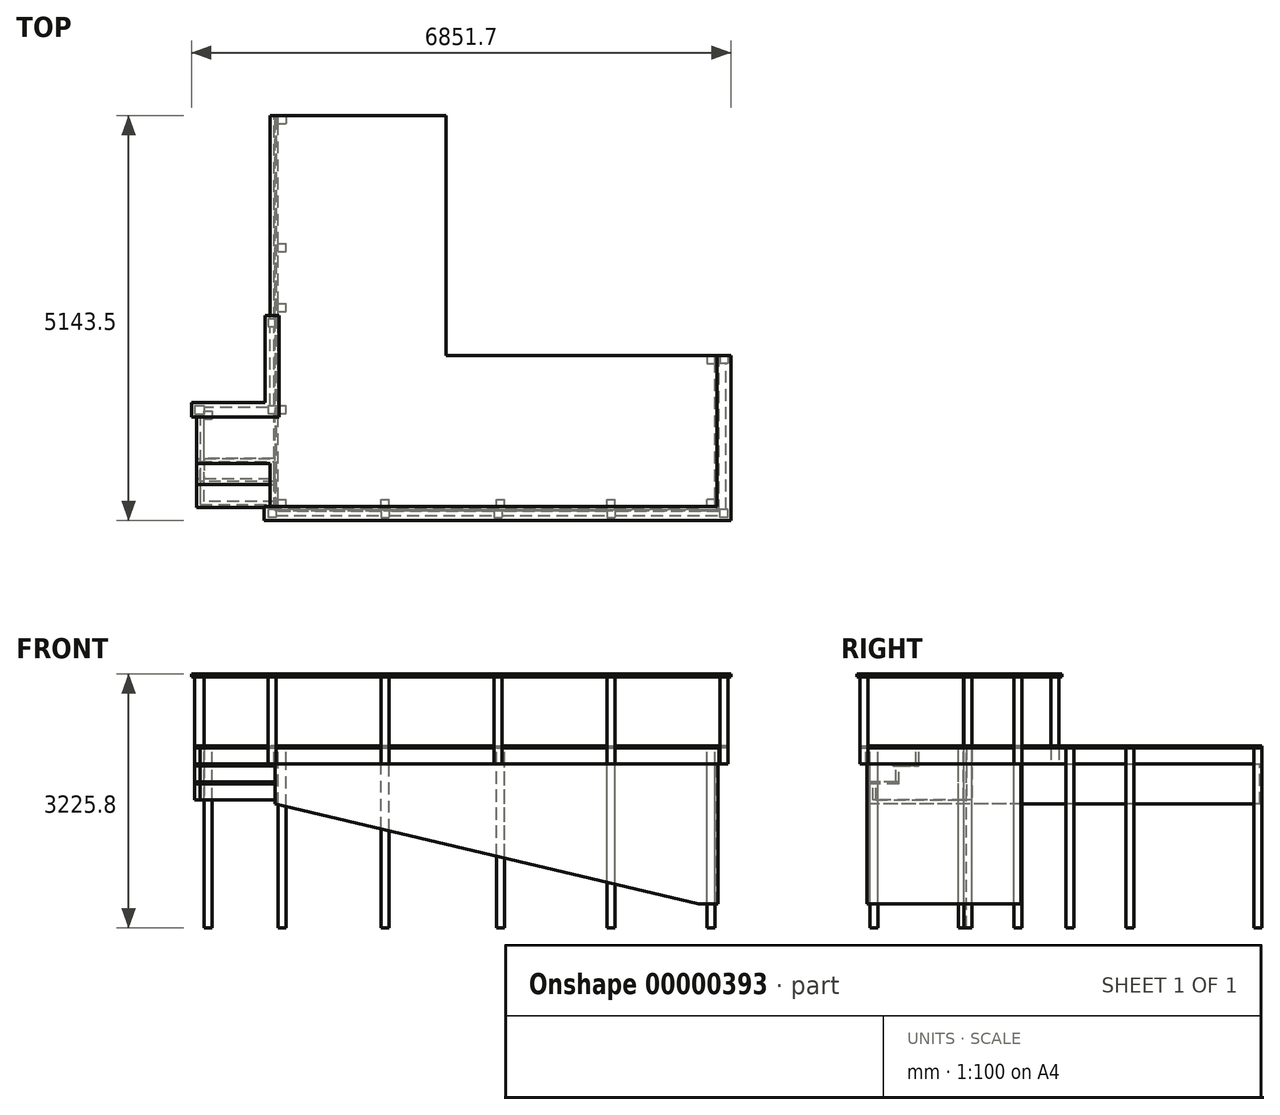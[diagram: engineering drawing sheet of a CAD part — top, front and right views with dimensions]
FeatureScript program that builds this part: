
annotation { "Feature Type Name" : "Feature", "Feature Type Description" : "" }
export const myFeature = defineFeature(function(context is Context, id is Id, definition is map)
    precondition{}
    {
        {
            var Q0;
            Q0=qCreatedBy(makeId("Top.planeOp"),FACE);
            var sketch = newSketch(context, id + "F0", { "sketchPlane" : qUnion([Q0])});
            skLineSegment(sketch, "E0.bottom", {"start": v(0, 0) * mm, "end": v(5791.2, 0) * mm});
            skLineSegment(sketch, "E0.top", {"start": v(2235.2, 2032) * mm, "end": v(5791.2, 2032) * mm});
            skLineSegment(sketch, "E0.right", {"start": v(5791.2, 0) * mm, "end": v(5791.2, 2032) * mm});
            skLineSegment(sketch, "E1.top", {"start": v(2235.2, 5080) * mm, "end": v(0, 5080) * mm});
            skLineSegment(sketch, "E1.left", {"start": v(2235.2, 2032) * mm, "end": v(2235.2, 5080) * mm});
            skLineSegment(sketch, "E2", {"start": v(0, 0) * mm, "end": v(0, 5080) * mm});
            skSolve(sketch);
        }
        {
            var Q0;
            Q0=makeQuery(id+"F0.imprint","IMPRINT",FACE,{"disambiguationData":[TD([[makeQuery(id+"F0.imprint","IMPRINT",EDGE,{"derivedFrom":sQuery(id+"F0.wireOp",EDGE,"E0.bottom")}),1.0]])]});
            extrude(context, id + "F1", {"entities" : qUnion([Q0]), "depth" : 25.4 * mm});
        }
        {
            var Q0;
            Q0=makeQuery(id+"F1.opExtrude","CAP_FACE",FACE,{"disambiguationData":[OSD([sQuery(id+"F0.wireOp",EDGE,"E0.bottom"),sQuery(id+"F0.wireOp",EDGE,"E0.top"),sQuery(id+"F0.wireOp",EDGE,"E0.right"),sQuery(id+"F0.wireOp",EDGE,"E1.top"),sQuery(id+"F0.wireOp",EDGE,"E1.left"),sQuery(id+"F0.wireOp",EDGE,"E2")])],"isStart":true});
            var sketch = newSketch(context, id + "F2", { "sketchPlane" : qUnion([Q0])});
            skLineSegment(sketch, "E3.bottom", {"start": v(5701.33, -50.8) * mm, "end": v(50.8, -50.8) * mm});
            skLineSegment(sketch, "E3.top", {"start": v(5650.53, -101.6) * mm, "end": v(101.6, -101.6) * mm});
            skLineSegment(sketch, "E3.left", {"start": v(5701.33, -50.8) * mm, "end": v(5701.33, -101.6) * mm});
            skLineSegment(sketch, "E3.right", {"start": v(50.8, -50.8) * mm, "end": v(50.8, -101.6) * mm});
            skLineSegment(sketch, "E4.top", {"start": v(50.8, -5080) * mm, "end": v(101.6, -5080) * mm});
            skLineSegment(sketch, "E4.left", {"start": v(50.8, -101.6) * mm, "end": v(50.8, -5080) * mm});
            skLineSegment(sketch, "E4.right", {"start": v(101.6, -101.6) * mm, "end": v(101.6, -5080) * mm});
            skLineSegment(sketch, "E5.top", {"start": v(5701.33, -2032) * mm, "end": v(5650.53, -2032) * mm});
            skLineSegment(sketch, "E5.left", {"start": v(5701.33, -101.6) * mm, "end": v(5701.33, -2032) * mm});
            skLineSegment(sketch, "E5.right", {"start": v(5650.53, -101.6) * mm, "end": v(5650.53, -2032) * mm});
            skSolve(sketch);
        }
        {
            var Q0;
            Q0=makeQuery(id+"F2.imprint","IMPRINT",FACE,{"disambiguationData":[TD([[makeQuery(id+"F2.imprint","IMPRINT",EDGE,{"derivedFrom":sQuery(id+"F2.wireOp",EDGE,"E3.bottom")}),1.0]])]});
            extrude(context, id + "F3", {"entities" : qUnion([Q0]), "operationType" : NewBodyOperationType.ADD, "depth" : 203.2 * mm});
        }
        {
            var Q0;
            Q0=makeQuery(id+"F1.opExtrude","CAP_FACE",FACE,{"disambiguationData":[OSD([sQuery(id+"F0.wireOp",EDGE,"E0.bottom"),sQuery(id+"F0.wireOp",EDGE,"E0.top"),sQuery(id+"F0.wireOp",EDGE,"E0.right"),sQuery(id+"F0.wireOp",EDGE,"E1.top"),sQuery(id+"F0.wireOp",EDGE,"E1.left"),sQuery(id+"F0.wireOp",EDGE,"E2")])],"isStart":false});
            var sketch = newSketch(context, id + "F4", { "sketchPlane" : qUnion([Q0])});
            skLineSegment(sketch, "E6.bottom", {"start": v(5816.6, -25.4) * mm, "end": v(5715, -25.4) * mm});
            skLineSegment(sketch, "E6.top", {"start": v(5816.6, 76.2) * mm, "end": v(5715, 76.2) * mm});
            skLineSegment(sketch, "E6.left", {"start": v(5816.6, -25.4) * mm, "end": v(5816.6, 76.2) * mm});
            skLineSegment(sketch, "E6.right", {"start": v(5715, -25.4) * mm, "end": v(5715, 76.2) * mm});
            skLineSegment(sketch, "E7.bottom", {"start": v(5816.6, 2032) * mm, "end": v(5715, 2032) * mm});
            skLineSegment(sketch, "E7.top", {"start": v(5816.6, 1930.4) * mm, "end": v(5715, 1930.4) * mm});
            skLineSegment(sketch, "E7.left", {"start": v(5816.6, 2032) * mm, "end": v(5816.6, 1930.4) * mm});
            skLineSegment(sketch, "E7.right", {"start": v(5715, 2032) * mm, "end": v(5715, 1930.4) * mm});
            skLineSegment(sketch, "E8.bottom", {"start": v(4279.9, 76.2) * mm, "end": v(4381.5, 76.2) * mm});
            skLineSegment(sketch, "E8.top", {"start": v(4279.9, -25.4) * mm, "end": v(4381.5, -25.4) * mm});
            skLineSegment(sketch, "E8.left", {"start": v(4279.9, 76.2) * mm, "end": v(4279.9, -25.4) * mm});
            skLineSegment(sketch, "E8.right", {"start": v(4381.5, 76.2) * mm, "end": v(4381.5, -25.4) * mm});
            skLineSegment(sketch, "E9.bottom", {"start": v(2844.8, 76.2) * mm, "end": v(2946.4, 76.2) * mm});
            skLineSegment(sketch, "E9.top", {"start": v(2844.8, -25.4) * mm, "end": v(2946.4, -25.4) * mm});
            skLineSegment(sketch, "E9.left", {"start": v(2844.8, 76.2) * mm, "end": v(2844.8, -25.4) * mm});
            skLineSegment(sketch, "E9.right", {"start": v(2946.4, 76.2) * mm, "end": v(2946.4, -25.4) * mm});
            skLineSegment(sketch, "E10.bottom", {"start": v(1409.7, 76.2) * mm, "end": v(1511.3, 76.2) * mm});
            skLineSegment(sketch, "E10.top", {"start": v(1409.7, -25.4) * mm, "end": v(1511.3, -25.4) * mm});
            skLineSegment(sketch, "E10.left", {"start": v(1409.7, 76.2) * mm, "end": v(1409.7, -25.4) * mm});
            skLineSegment(sketch, "E10.right", {"start": v(1511.3, 76.2) * mm, "end": v(1511.3, -25.4) * mm});
            skLineSegment(sketch, "E11.bottom", {"start": v(76.2, 76.2) * mm, "end": v(-25.4, 76.2) * mm});
            skLineSegment(sketch, "E11.top", {"start": v(76.2, -25.4) * mm, "end": v(-25.4, -25.4) * mm});
            skLineSegment(sketch, "E11.left", {"start": v(76.2, 76.2) * mm, "end": v(76.2, -25.4) * mm});
            skLineSegment(sketch, "E11.right", {"start": v(-25.4, 76.2) * mm, "end": v(-25.4, -25.4) * mm});
            skLineSegment(sketch, "E12.bottom", {"start": v(-25.4, 1397) * mm, "end": v(76.2, 1397) * mm});
            skLineSegment(sketch, "E12.top", {"start": v(-25.4, 1295.4) * mm, "end": v(76.2, 1295.4) * mm});
            skLineSegment(sketch, "E12.left", {"start": v(-25.4, 1397) * mm, "end": v(-25.4, 1295.4) * mm});
            skLineSegment(sketch, "E12.right", {"start": v(76.2, 1397) * mm, "end": v(76.2, 1295.4) * mm});
            skLineSegment(sketch, "E13.bottom", {"start": v(-25.4, 2500.64) * mm, "end": v(76.2, 2500.64) * mm});
            skLineSegment(sketch, "E13.top", {"start": v(-25.4, 2399.04) * mm, "end": v(76.2, 2399.04) * mm});
            skLineSegment(sketch, "E13.left", {"start": v(-25.4, 2500.64) * mm, "end": v(-25.4, 2399.04) * mm});
            skLineSegment(sketch, "E13.right", {"start": v(76.2, 2500.64) * mm, "end": v(76.2, 2399.04) * mm});
            skLineSegment(sketch, "E14.bottom", {"start": v(-958.9, 1397) * mm, "end": v(-838.2, 1397) * mm});
            skLineSegment(sketch, "E14.top", {"start": v(-958.9, 1290.4) * mm, "end": v(-838.2, 1290.4) * mm});
            skLineSegment(sketch, "E14.left", {"start": v(-958.9, 1397) * mm, "end": v(-958.9, 1290.4) * mm});
            skLineSegment(sketch, "E14.right", {"start": v(-838.2, 1397) * mm, "end": v(-838.2, 1290.4) * mm});
            skLineSegment(sketch, "E15", {"start": v(76.2, 76.2) * mm, "end": v(1409.7, 76.2) * mm, "construction": true});
            skLineSegment(sketch, "E16", {"start": v(2844.8, 76.2) * mm, "end": v(1511.3, 76.2) * mm, "construction": true});
            skLineSegment(sketch, "E17", {"start": v(4279.9, 76.2) * mm, "end": v(2946.4, 76.2) * mm, "construction": true});
            skLineSegment(sketch, "E18", {"start": v(5715, 76.2) * mm, "end": v(4381.5, 76.2) * mm, "construction": true});
            skSolve(sketch);
        }
        {
            var Q0;
            {var subQ6=sQuery(id+"F4.wireOp",EDGE,"E7.left");var subQ13=sQuery(id+"F4.wireOp",EDGE,"E8.top");var subQ19=sQuery(id+"F4.wireOp",EDGE,"E9.top");var subQ22=sQuery(id+"F4.wireOp",EDGE,"E10.top");var subQ32=sQuery(id+"F4.wireOp",EDGE,"E12.left");var subQ38=sQuery(id+"F4.wireOp",EDGE,"E13.left");var subQ39=sQuery(id+"F4.wireOp",EDGE,"E7.right");var subQ40=sQuery(id+"F4.wireOp",EDGE,"E8.bottom");var subQ41=sQuery(id+"F4.wireOp",EDGE,"E9.bottom");var subQ42=sQuery(id+"F4.wireOp",EDGE,"E10.bottom");var subQ43=sQuery(id+"F4.wireOp",EDGE,"E12.right");var subQ44=sQuery(id+"F4.wireOp",EDGE,"E13.right");var subQ45=sQuery(id+"F4.wireOp",EDGE,"E6.right");var subQ49=sQuery(id+"F4.wireOp",EDGE,"E6.bottom");var subQ50=sQuery(id+"F4.wireOp",EDGE,"E6.top");var subQ54=sQuery(id+"F4.wireOp",EDGE,"E11.bottom");var subQ58=sQuery(id+"F4.wireOp",EDGE,"E11.left");var subQ62=sQuery(id+"F4.wireOp",EDGE,"E11.top");var subQ63=makeQuery(id+"F4.imprint","INTERSECT",VERTEX,{"derivedFrom":[subQ50,subQ45]});var subQ64=makeQuery(id+"F4.imprint","INTERSECT",VERTEX,{"derivedFrom":[subQ54,subQ58]});Q0=qUnion([makeQuery(id+"F4.imprint","IMPRINT",FACE,{"disambiguationData":[TD([[makeQuery(id+"F4.imprint","IMPRINT",EDGE,{"derivedFrom":sQuery(id+"F4.wireOp",EDGE,"E14.bottom")}),-1.0]])]}),makeQuery(id+"F4.imprint","IMPRINT",FACE,{"disambiguationData":[TD([[makeQuery(id+"F4.imprint","IMPRINT",EDGE,{"derivedFrom":subQ6}),-1.0]])]}),makeQuery(id+"F4.imprint","IMPRINT",FACE,{"disambiguationData":[TD([[makeQuery(id+"F4.imprint","IMPRINT",EDGE,{"derivedFrom":subQ13}),1.0]])]}),makeQuery(id+"F4.imprint","IMPRINT",FACE,{"disambiguationData":[TD([[makeQuery(id+"F4.imprint","IMPRINT",EDGE,{"derivedFrom":subQ19}),1.0]])]}),makeQuery(id+"F4.imprint","IMPRINT",FACE,{"disambiguationData":[TD([[makeQuery(id+"F4.imprint","IMPRINT",EDGE,{"derivedFrom":subQ22}),1.0]])]}),makeQuery(id+"F4.imprint","IMPRINT",FACE,{"disambiguationData":[TD([[makeQuery(id+"F4.imprint","IMPRINT",EDGE,{"derivedFrom":subQ32}),1.0]])]}),makeQuery(id+"F4.imprint","IMPRINT",FACE,{"disambiguationData":[TD([[makeQuery(id+"F4.imprint","IMPRINT",EDGE,{"derivedFrom":subQ38}),1.0]])]}),makeQuery(id+"F4.imprint","IMPRINT",FACE,{"disambiguationData":[TD([[makeQuery(id+"F4.imprint","IMPRINT",EDGE,{"derivedFrom":subQ39}),1.0]])]}),makeQuery(id+"F4.imprint","IMPRINT",FACE,{"disambiguationData":[TD([[makeQuery(id+"F4.imprint","IMPRINT",EDGE,{"derivedFrom":subQ40}),-1.0]])]}),makeQuery(id+"F4.imprint","IMPRINT",FACE,{"disambiguationData":[TD([[makeQuery(id+"F4.imprint","IMPRINT",EDGE,{"derivedFrom":subQ41}),-1.0]])]}),makeQuery(id+"F4.imprint","IMPRINT",FACE,{"disambiguationData":[TD([[makeQuery(id+"F4.imprint","IMPRINT",EDGE,{"derivedFrom":subQ42}),-1.0]])]}),makeQuery(id+"F4.imprint","IMPRINT",FACE,{"disambiguationData":[TD([[makeQuery(id+"F4.imprint","IMPRINT",EDGE,{"derivedFrom":subQ43}),-1.0]])]}),makeQuery(id+"F4.imprint","IMPRINT",FACE,{"disambiguationData":[TD([[makeQuery(id+"F4.imprint","IMPRINT",EDGE,{"derivedFrom":subQ44}),-1.0]])]}),makeQuery(id+"F4.imprint","IMPRINT",FACE,{"disambiguationData":[TD([[makeQuery(id+"F4.imprint","IMPRINT",EDGE,{"derivedFrom":subQ49}),-1.0]])]}),makeQuery(id+"F4.imprint","IMPRINT",FACE,{"disambiguationData":[TD([[makeQuery(id+"F4.imprint","IMPRINT",EDGE,{"derivedFrom":subQ62}),-1.0]])]}),makeQuery(id+"F4.imprint","IMPRINT",FACE,{"disambiguationData":[TD([[makeQuery(id+"F4.imprint","IMPRINT",EDGE,{"disambiguationData":[TD([[subQ63,1.0]])],"derivedFrom":subQ50}),1.0]])]}),makeQuery(id+"F4.imprint","IMPRINT",FACE,{"disambiguationData":[TD([[makeQuery(id+"F4.imprint","IMPRINT",EDGE,{"disambiguationData":[TD([[subQ64,-1.0]])],"derivedFrom":subQ54}),1.0]])]})]);}
            extrude(context, id + "F5", {"entities" : qUnion([Q0]), "operationType" : NewBodyOperationType.ADD, "depth" : 914.4 * mm});
        }
        {
            var Q0;
            {var subQ6=sQuery(id+"F4.wireOp",EDGE,"E7.left");var subQ13=sQuery(id+"F4.wireOp",EDGE,"E8.top");var subQ19=sQuery(id+"F4.wireOp",EDGE,"E9.top");var subQ22=sQuery(id+"F4.wireOp",EDGE,"E10.top");var subQ32=sQuery(id+"F4.wireOp",EDGE,"E12.left");var subQ38=sQuery(id+"F4.wireOp",EDGE,"E13.left");var subQ39=sQuery(id+"F4.wireOp",EDGE,"E7.right");var subQ40=sQuery(id+"F4.wireOp",EDGE,"E8.bottom");var subQ41=sQuery(id+"F4.wireOp",EDGE,"E9.bottom");var subQ42=sQuery(id+"F4.wireOp",EDGE,"E10.bottom");var subQ43=sQuery(id+"F4.wireOp",EDGE,"E12.right");var subQ44=sQuery(id+"F4.wireOp",EDGE,"E13.right");var subQ45=sQuery(id+"F4.wireOp",EDGE,"E6.right");var subQ49=sQuery(id+"F4.wireOp",EDGE,"E6.bottom");var subQ50=sQuery(id+"F4.wireOp",EDGE,"E6.top");var subQ54=sQuery(id+"F4.wireOp",EDGE,"E11.bottom");var subQ58=sQuery(id+"F4.wireOp",EDGE,"E11.left");var subQ62=sQuery(id+"F4.wireOp",EDGE,"E11.top");var subQ63=makeQuery(id+"F4.imprint","INTERSECT",VERTEX,{"derivedFrom":[subQ50,subQ45]});var subQ64=makeQuery(id+"F4.imprint","INTERSECT",VERTEX,{"derivedFrom":[subQ54,subQ58]});Q0=qUnion([makeQuery(id+"F4.imprint","IMPRINT",FACE,{"disambiguationData":[TD([[makeQuery(id+"F4.imprint","IMPRINT",EDGE,{"derivedFrom":sQuery(id+"F4.wireOp",EDGE,"E14.bottom")}),-1.0]])]}),makeQuery(id+"F4.imprint","IMPRINT",FACE,{"disambiguationData":[TD([[makeQuery(id+"F4.imprint","IMPRINT",EDGE,{"derivedFrom":subQ6}),-1.0]])]}),makeQuery(id+"F4.imprint","IMPRINT",FACE,{"disambiguationData":[TD([[makeQuery(id+"F4.imprint","IMPRINT",EDGE,{"derivedFrom":subQ13}),1.0]])]}),makeQuery(id+"F4.imprint","IMPRINT",FACE,{"disambiguationData":[TD([[makeQuery(id+"F4.imprint","IMPRINT",EDGE,{"derivedFrom":subQ19}),1.0]])]}),makeQuery(id+"F4.imprint","IMPRINT",FACE,{"disambiguationData":[TD([[makeQuery(id+"F4.imprint","IMPRINT",EDGE,{"derivedFrom":subQ22}),1.0]])]}),makeQuery(id+"F4.imprint","IMPRINT",FACE,{"disambiguationData":[TD([[makeQuery(id+"F4.imprint","IMPRINT",EDGE,{"derivedFrom":subQ32}),1.0]])]}),makeQuery(id+"F4.imprint","IMPRINT",FACE,{"disambiguationData":[TD([[makeQuery(id+"F4.imprint","IMPRINT",EDGE,{"derivedFrom":subQ38}),1.0]])]}),makeQuery(id+"F4.imprint","IMPRINT",FACE,{"disambiguationData":[TD([[makeQuery(id+"F4.imprint","IMPRINT",EDGE,{"derivedFrom":subQ39}),1.0]])]}),makeQuery(id+"F4.imprint","IMPRINT",FACE,{"disambiguationData":[TD([[makeQuery(id+"F4.imprint","IMPRINT",EDGE,{"derivedFrom":subQ40}),-1.0]])]}),makeQuery(id+"F4.imprint","IMPRINT",FACE,{"disambiguationData":[TD([[makeQuery(id+"F4.imprint","IMPRINT",EDGE,{"derivedFrom":subQ41}),-1.0]])]}),makeQuery(id+"F4.imprint","IMPRINT",FACE,{"disambiguationData":[TD([[makeQuery(id+"F4.imprint","IMPRINT",EDGE,{"derivedFrom":subQ42}),-1.0]])]}),makeQuery(id+"F4.imprint","IMPRINT",FACE,{"disambiguationData":[TD([[makeQuery(id+"F4.imprint","IMPRINT",EDGE,{"derivedFrom":subQ43}),-1.0]])]}),makeQuery(id+"F4.imprint","IMPRINT",FACE,{"disambiguationData":[TD([[makeQuery(id+"F4.imprint","IMPRINT",EDGE,{"derivedFrom":subQ44}),-1.0]])]}),makeQuery(id+"F4.imprint","IMPRINT",FACE,{"disambiguationData":[TD([[makeQuery(id+"F4.imprint","IMPRINT",EDGE,{"derivedFrom":subQ49}),-1.0]])]}),makeQuery(id+"F4.imprint","IMPRINT",FACE,{"disambiguationData":[TD([[makeQuery(id+"F4.imprint","IMPRINT",EDGE,{"derivedFrom":subQ62}),-1.0]])]}),makeQuery(id+"F4.imprint","IMPRINT",FACE,{"disambiguationData":[TD([[makeQuery(id+"F4.imprint","IMPRINT",EDGE,{"disambiguationData":[TD([[subQ63,1.0]])],"derivedFrom":subQ50}),1.0]])]}),makeQuery(id+"F4.imprint","IMPRINT",FACE,{"disambiguationData":[TD([[makeQuery(id+"F4.imprint","IMPRINT",EDGE,{"disambiguationData":[TD([[subQ64,-1.0]])],"derivedFrom":subQ54}),1.0]])]})]);}
            var Q1;
            Q1=makeQuery(id+"F3.opExtrude","CAP_FACE",FACE,{"disambiguationData":[OSD([sQuery(id+"F2.wireOp",EDGE,"E3.bottom"),sQuery(id+"F2.wireOp",EDGE,"E3.top"),sQuery(id+"F2.wireOp",EDGE,"E3.left"),sQuery(id+"F2.wireOp",EDGE,"E3.right"),sQuery(id+"F2.wireOp",EDGE,"E4.top"),sQuery(id+"F2.wireOp",EDGE,"E4.left"),sQuery(id+"F2.wireOp",EDGE,"E4.right"),sQuery(id+"F2.wireOp",EDGE,"E5.top"),sQuery(id+"F2.wireOp",EDGE,"E5.left"),sQuery(id+"F2.wireOp",EDGE,"E5.right")])],"isStart":false});
            extrude(context, id + "F6", {"entities" : qUnion([Q0]), "operationType" : NewBodyOperationType.ADD, "endBound" : BoundingType.UP_TO_SURFACE, "oppositeDirection" : true, "endBoundEntityFace" : qUnion([Q1]), "depth" : 25.4 * mm});
        }
        {
            var Q0;
            Q0=makeQuery(id+"F1.opExtrude","CAP_FACE",FACE,{"disambiguationData":[OSD([sQuery(id+"F0.wireOp",EDGE,"E0.bottom"),sQuery(id+"F0.wireOp",EDGE,"E0.top"),sQuery(id+"F0.wireOp",EDGE,"E0.right"),sQuery(id+"F0.wireOp",EDGE,"E1.top"),sQuery(id+"F0.wireOp",EDGE,"E1.left"),sQuery(id+"F0.wireOp",EDGE,"E2")])],"isStart":false});
            var sketch = newSketch(context, id + "F7", { "sketchPlane" : qUnion([Q0])});
            skLineSegment(sketch, "E19.bottom", {"start": v(-933.5, 1371.6) * mm, "end": v(0, 1371.6) * mm});
            skLineSegment(sketch, "E19.top", {"start": v(-933.5, 660.4) * mm, "end": v(0, 660.4) * mm});
            skLineSegment(sketch, "E19.left", {"start": v(-933.5, 1371.6) * mm, "end": v(-933.5, 660.4) * mm});
            skLineSegment(sketch, "E19.right", {"start": v(0, 1371.6) * mm, "end": v(0, 660.4) * mm});
            skSolve(sketch);
        }
        {
            var Q0;
            {var subQ1=sQuery(id+"F7.wireOp",EDGE,"E19.bottom");Q0=makeQuery(id+"F7.imprint","IMPRINT",FACE,{"disambiguationData":[TD([[makeQuery(id+"F7.imprint","IMPRINT",EDGE,{"derivedFrom":subQ1}),-1.0]])]});}
            var Q1;
            {var subQ0=sQuery(id+"F0.wireOp",EDGE,"E0.top");var subQ1=sQuery(id+"F0.wireOp",EDGE,"E1.top");var subQ2=sQuery(id+"F0.wireOp",EDGE,"E1.left");Q1=makeQuery(id+"F3.boolean.opBoolean","SPLIT",FACE,{"disambiguationData":[TD([makeQuery(id+"F1.opExtrude","SWEPT_FACE",FACE,{"disambiguationData":[OSD([subQ2])]})])],"derivedFrom":makeQuery(id+"F1.opExtrude","CAP_FACE",FACE,{"disambiguationData":[OSD([sQuery(id+"F0.wireOp",EDGE,"E0.bottom"),subQ0,sQuery(id+"F0.wireOp",EDGE,"E0.right"),subQ1,subQ2,sQuery(id+"F0.wireOp",EDGE,"E2")])],"isStart":true})});}
            extrude(context, id + "F8", {"entities" : qUnion([Q0]), "operationType" : NewBodyOperationType.ADD, "endBound" : BoundingType.UP_TO_SURFACE, "oppositeDirection" : true, "endBoundEntityFace" : qUnion([Q1]), "depth" : 25.4 * mm});
        }
        {
            var Q0;
            Q0=makeQuery(id+"F5.opExtrude","CAP_FACE",FACE,{"disambiguationData":[OSD([sQuery(id+"F4.wireOp",EDGE,"E11.bottom"),sQuery(id+"F4.wireOp",EDGE,"E11.top"),sQuery(id+"F4.wireOp",EDGE,"E11.left"),sQuery(id+"F4.wireOp",EDGE,"E11.right")])],"isStart":false});
            var sketch = newSketch(context, id + "F9", { "sketchPlane" : qUnion([Q0])});
            skLineSegment(sketch, "E20.bottom", {"start": v(-76.2, 114.3) * mm, "end": v(5676.9, 114.3) * mm});
            skLineSegment(sketch, "E20.top", {"start": v(-76.2, -63.5) * mm, "end": v(5854.7, -63.5) * mm});
            skLineSegment(sketch, "E20.left", {"start": v(-76.2, 114.3) * mm, "end": v(-76.2, -63.5) * mm});
            skLineSegment(sketch, "E20.right", {"start": v(5854.7, 114.3) * mm, "end": v(5854.7, -63.5) * mm});
            skLineSegment(sketch, "E21.bottom", {"start": v(5676.9, 2032) * mm, "end": v(5854.7, 2032) * mm});
            skLineSegment(sketch, "E21.left", {"start": v(5676.9, 2032) * mm, "end": v(5676.9, 114.3) * mm});
            skLineSegment(sketch, "E21.right", {"start": v(5854.7, 2032) * mm, "end": v(5854.7, 114.3) * mm});
            skLineSegment(sketch, "E22", {"start": v(-997, 1435.1) * mm, "end": v(-63.5, 1435.1) * mm});
            skLineSegment(sketch, "E23", {"start": v(-63.5, 1435.1) * mm, "end": v(-63.5, 2538.74) * mm});
            skLineSegment(sketch, "E24", {"start": v(-63.5, 2538.74) * mm, "end": v(114.3, 2538.74) * mm});
            skLineSegment(sketch, "E25", {"start": v(114.3, 2538.74) * mm, "end": v(114.3, 1252.3) * mm});
            skLineSegment(sketch, "E26", {"start": v(114.3, 1252.3) * mm, "end": v(-997, 1252.3) * mm});
            skLineSegment(sketch, "E27", {"start": v(-997, 1252.3) * mm, "end": v(-997, 1435.1) * mm});
            skSolve(sketch);
        }
        {
            var Q0;
            Q0=makeQuery(id+"F9.imprint","IMPRINT",FACE,{"disambiguationData":[TD([[makeQuery(id+"F9.imprint","IMPRINT",EDGE,{"derivedFrom":sQuery(id+"F9.wireOp",EDGE,"E22")}),-1.0]])]});
            var Q1;
            Q1=makeQuery(id+"F9.imprint","IMPRINT",FACE,{"disambiguationData":[TD([[makeQuery(id+"F9.imprint","IMPRINT",EDGE,{"derivedFrom":sQuery(id+"F9.wireOp",EDGE,"E20.bottom")}),-1.0]])]});
            extrude(context, id + "F10", {"entities" : qUnion([Q0, Q1]), "operationType" : NewBodyOperationType.ADD, "oppositeDirection" : true, "depth" : 38.1 * mm});
        }
        {
            var Q0;
            {var subQ0=sQuery(id+"F0.wireOp",EDGE,"E0.top");var subQ1=sQuery(id+"F0.wireOp",EDGE,"E1.top");var subQ2=sQuery(id+"F0.wireOp",EDGE,"E1.left");Q0=makeQuery(id+"F3.boolean.opBoolean","SPLIT",FACE,{"disambiguationData":[TD([makeQuery(id+"F1.opExtrude","SWEPT_FACE",FACE,{"disambiguationData":[OSD([subQ2])]})])],"derivedFrom":makeQuery(id+"F1.opExtrude","CAP_FACE",FACE,{"disambiguationData":[OSD([sQuery(id+"F0.wireOp",EDGE,"E0.bottom"),subQ0,sQuery(id+"F0.wireOp",EDGE,"E0.right"),subQ1,subQ2,sQuery(id+"F0.wireOp",EDGE,"E2")])],"isStart":true})});}
            var sketch = newSketch(context, id + "F11", { "sketchPlane" : qUnion([Q0])});
            skLineSegment(sketch, "E28.bottom", {"start": v(5548.93, -2032) * mm, "end": v(5650.53, -2032) * mm});
            skLineSegment(sketch, "E28.top", {"start": v(5548.93, -1930.4) * mm, "end": v(5650.53, -1930.4) * mm});
            skLineSegment(sketch, "E28.left", {"start": v(5548.93, -2032) * mm, "end": v(5548.93, -1930.4) * mm});
            skLineSegment(sketch, "E28.right", {"start": v(5650.53, -2032) * mm, "end": v(5650.53, -1930.4) * mm});
            skLineSegment(sketch, "E29.bottom", {"start": v(5650.53, -101.6) * mm, "end": v(5548.93, -101.6) * mm});
            skLineSegment(sketch, "E29.top", {"start": v(5650.53, -203.2) * mm, "end": v(5548.93, -203.2) * mm});
            skLineSegment(sketch, "E29.left", {"start": v(5650.53, -101.6) * mm, "end": v(5650.53, -203.2) * mm});
            skLineSegment(sketch, "E29.right", {"start": v(5548.93, -101.6) * mm, "end": v(5548.93, -203.2) * mm});
            skLineSegment(sketch, "E30.bottom", {"start": v(4279.9, -101.6) * mm, "end": v(4381.5, -101.6) * mm});
            skLineSegment(sketch, "E30.top", {"start": v(4279.9, -203.2) * mm, "end": v(4381.5, -203.2) * mm});
            skLineSegment(sketch, "E30.left", {"start": v(4279.9, -101.6) * mm, "end": v(4279.9, -203.2) * mm});
            skLineSegment(sketch, "E30.right", {"start": v(4381.5, -101.6) * mm, "end": v(4381.5, -203.2) * mm});
            skLineSegment(sketch, "E31.bottom", {"start": v(2876.07, -101.6) * mm, "end": v(2977.67, -101.6) * mm});
            skLineSegment(sketch, "E31.top", {"start": v(2876.07, -203.2) * mm, "end": v(2977.67, -203.2) * mm});
            skLineSegment(sketch, "E31.left", {"start": v(2876.07, -101.6) * mm, "end": v(2876.07, -203.2) * mm});
            skLineSegment(sketch, "E31.right", {"start": v(2977.67, -101.6) * mm, "end": v(2977.67, -203.2) * mm});
            skLineSegment(sketch, "E32.bottom", {"start": v(1409.7, -101.6) * mm, "end": v(1511.3, -101.6) * mm});
            skLineSegment(sketch, "E32.top", {"start": v(1409.7, -203.2) * mm, "end": v(1511.3, -203.2) * mm});
            skLineSegment(sketch, "E32.left", {"start": v(1409.7, -101.6) * mm, "end": v(1409.7, -203.2) * mm});
            skLineSegment(sketch, "E32.right", {"start": v(1511.3, -101.6) * mm, "end": v(1511.3, -203.2) * mm});
            skLineSegment(sketch, "E33.bottom", {"start": v(101.6, -101.6) * mm, "end": v(203.2, -101.6) * mm});
            skLineSegment(sketch, "E33.top", {"start": v(101.6, -203.2) * mm, "end": v(203.2, -203.2) * mm});
            skLineSegment(sketch, "E33.left", {"start": v(101.6, -101.6) * mm, "end": v(101.6, -203.2) * mm});
            skLineSegment(sketch, "E33.right", {"start": v(203.2, -101.6) * mm, "end": v(203.2, -203.2) * mm});
            skLineSegment(sketch, "E34.bottom", {"start": v(101.6, -1295.4) * mm, "end": v(203.2, -1295.4) * mm});
            skLineSegment(sketch, "E34.top", {"start": v(101.6, -1397) * mm, "end": v(203.2, -1397) * mm});
            skLineSegment(sketch, "E34.left", {"start": v(101.6, -1295.4) * mm, "end": v(101.6, -1397) * mm});
            skLineSegment(sketch, "E34.right", {"start": v(203.2, -1295.4) * mm, "end": v(203.2, -1397) * mm});
            skLineSegment(sketch, "E35.bottom", {"start": v(101.6, -2590.8) * mm, "end": v(203.2, -2590.8) * mm});
            skLineSegment(sketch, "E35.top", {"start": v(101.6, -2692.4) * mm, "end": v(203.2, -2692.4) * mm});
            skLineSegment(sketch, "E35.left", {"start": v(101.6, -2590.8) * mm, "end": v(101.6, -2692.4) * mm});
            skLineSegment(sketch, "E35.right", {"start": v(203.2, -2590.8) * mm, "end": v(203.2, -2692.4) * mm});
            skLineSegment(sketch, "E36.bottom", {"start": v(101.6, -3350.61) * mm, "end": v(203.2, -3350.61) * mm});
            skLineSegment(sketch, "E36.top", {"start": v(101.6, -3452.21) * mm, "end": v(203.2, -3452.21) * mm});
            skLineSegment(sketch, "E36.left", {"start": v(101.6, -3350.61) * mm, "end": v(101.6, -3452.21) * mm});
            skLineSegment(sketch, "E36.right", {"start": v(203.2, -3350.61) * mm, "end": v(203.2, -3452.21) * mm});
            skLineSegment(sketch, "E37.bottom", {"start": v(101.6, -5080) * mm, "end": v(203.2, -5080) * mm});
            skLineSegment(sketch, "E37.top", {"start": v(101.6, -4978.4) * mm, "end": v(203.2, -4978.4) * mm});
            skLineSegment(sketch, "E37.left", {"start": v(101.6, -5080) * mm, "end": v(101.6, -4978.4) * mm});
            skLineSegment(sketch, "E37.right", {"start": v(203.2, -5080) * mm, "end": v(203.2, -4978.4) * mm});
            skLineSegment(sketch, "E38.bottom", {"start": v(-839.2, -1328.5) * mm, "end": v(-737.6, -1328.5) * mm});
            skLineSegment(sketch, "E38.top", {"start": v(-839.2, -1226.9) * mm, "end": v(-737.6, -1226.9) * mm});
            skLineSegment(sketch, "E38.left", {"start": v(-839.2, -1328.5) * mm, "end": v(-839.2, -1226.9) * mm});
            skLineSegment(sketch, "E38.right", {"start": v(-737.6, -1328.5) * mm, "end": v(-737.6, -1226.9) * mm});
            skSolve(sketch);
        }
        {
            var Q0;
            {Q0=qUnion([makeQuery(id+"F11.imprint","IMPRINT",FACE,{"disambiguationData":[TD([[makeQuery(id+"F11.imprint","IMPRINT",EDGE,{"derivedFrom":sQuery(id+"F11.wireOp",EDGE,"E38.bottom")}),1.0]])]}),makeQuery(id+"F11.imprint","IMPRINT",FACE,{"disambiguationData":[TD([[makeQuery(id+"F11.imprint","IMPRINT",EDGE,{"derivedFrom":sQuery(id+"F11.wireOp",EDGE,"E28.bottom")}),1.0]])]}),makeQuery(id+"F11.imprint","IMPRINT",FACE,{"disambiguationData":[TD([[makeQuery(id+"F11.imprint","IMPRINT",EDGE,{"derivedFrom":sQuery(id+"F11.wireOp",EDGE,"E29.bottom")}),1.0]])]}),makeQuery(id+"F11.imprint","IMPRINT",FACE,{"disambiguationData":[TD([[makeQuery(id+"F11.imprint","IMPRINT",EDGE,{"derivedFrom":sQuery(id+"F11.wireOp",EDGE,"E30.bottom")}),1.0]])]}),makeQuery(id+"F11.imprint","IMPRINT",FACE,{"disambiguationData":[TD([[makeQuery(id+"F11.imprint","IMPRINT",EDGE,{"derivedFrom":sQuery(id+"F11.wireOp",EDGE,"E31.bottom")}),1.0]])]}),makeQuery(id+"F11.imprint","IMPRINT",FACE,{"disambiguationData":[TD([[makeQuery(id+"F11.imprint","IMPRINT",EDGE,{"derivedFrom":sQuery(id+"F11.wireOp",EDGE,"E32.bottom")}),1.0]])]}),makeQuery(id+"F11.imprint","IMPRINT",FACE,{"disambiguationData":[TD([[makeQuery(id+"F11.imprint","IMPRINT",EDGE,{"derivedFrom":sQuery(id+"F11.wireOp",EDGE,"E33.bottom")}),1.0]])]}),makeQuery(id+"F11.imprint","IMPRINT",FACE,{"disambiguationData":[TD([[makeQuery(id+"F11.imprint","IMPRINT",EDGE,{"derivedFrom":sQuery(id+"F11.wireOp",EDGE,"E34.bottom")}),-1.0]])]}),makeQuery(id+"F11.imprint","IMPRINT",FACE,{"disambiguationData":[TD([[makeQuery(id+"F11.imprint","IMPRINT",EDGE,{"derivedFrom":sQuery(id+"F11.wireOp",EDGE,"E35.bottom")}),-1.0]])]}),makeQuery(id+"F11.imprint","IMPRINT",FACE,{"disambiguationData":[TD([[makeQuery(id+"F11.imprint","IMPRINT",EDGE,{"derivedFrom":sQuery(id+"F11.wireOp",EDGE,"E36.bottom")}),-1.0]])]}),makeQuery(id+"F11.imprint","IMPRINT",FACE,{"disambiguationData":[TD([[makeQuery(id+"F11.imprint","IMPRINT",EDGE,{"derivedFrom":sQuery(id+"F11.wireOp",EDGE,"E37.bottom")}),-1.0]])]})]);}
            extrude(context, id + "F12", {"entities" : qUnion([Q0]), "operationType" : NewBodyOperationType.ADD, "depth" : 2286 * mm});
        }
        {
            var Q0;
            {var subQ0=sQuery(id+"F0.wireOp",EDGE,"E0.bottom");var subQ1=sQuery(id+"F0.wireOp",EDGE,"E0.top");var subQ2=sQuery(id+"F0.wireOp",EDGE,"E0.right");var subQ3=sQuery(id+"F0.wireOp",EDGE,"E1.top");var subQ4=sQuery(id+"F0.wireOp",EDGE,"E2");var subQ7=sQuery(id+"F4.wireOp",EDGE,"E11.bottom");Q0=makeQuery(id+"F8.boolean.opBoolean","MERGE",FACE,{"derivedFrom":[makeQuery(id+"F6.boolean.opBoolean","SPLIT",FACE,{"disambiguationData":[TD([makeQuery(id+"F5.opExtrude","SWEPT_FACE",FACE,{"disambiguationData":[OSD([subQ7])]})])],"derivedFrom":makeQuery(id+"F3.boolean.opBoolean","SPLIT",FACE,{"disambiguationData":[TD([makeQuery(id+"F1.opExtrude","SWEPT_FACE",FACE,{"disambiguationData":[OSD([subQ0])]})])],"derivedFrom":makeQuery(id+"F1.opExtrude","CAP_FACE",FACE,{"disambiguationData":[OSD([subQ0,subQ1,subQ2,subQ3,sQuery(id+"F0.wireOp",EDGE,"E1.left"),subQ4])],"isStart":true})})}),makeQuery(id+"F8.opExtrude","CAP_FACE",FACE,{"disambiguationData":[OSD([sQuery(id+"F7.wireOp",EDGE,"E19.bottom"),sQuery(id+"F7.wireOp",EDGE,"E19.top"),sQuery(id+"F7.wireOp",EDGE,"E19.left"),sQuery(id+"F7.wireOp",EDGE,"E19.right")])],"isStart":false})]});}
            var sketch = newSketch(context, id + "F13", { "sketchPlane" : qUnion([Q0])});
            skLineSegment(sketch, "E39", {"start": v(-886.35, -1290.4) * mm, "end": v(-886.35, -685.8) * mm});
            skLineSegment(sketch, "E40", {"start": v(-886.35, -685.8) * mm, "end": v(50.8, -685.8) * mm});
            skLineSegment(sketch, "E41", {"start": v(50.8, -685.8) * mm, "end": v(50.8, -723.9) * mm});
            skLineSegment(sketch, "E42", {"start": v(50.8, -723.9) * mm, "end": v(-838.7, -723.9) * mm});
            skLineSegment(sketch, "E43", {"start": v(-838.7, -723.9) * mm, "end": v(-838.7, -1290.4) * mm});
            skLineSegment(sketch, "E44", {"start": v(-838.7, -1290.4) * mm, "end": v(-886.35, -1290.4) * mm});
            skSolve(sketch);
        }
        {
            var Q0;
            {var subQ6=sQuery(id+"F13.wireOp",EDGE,"E39");Q0=makeQuery(id+"F13.imprint","IMPRINT",FACE,{"disambiguationData":[TD([[makeQuery(id+"F13.imprint","IMPRINT",EDGE,{"derivedFrom":subQ6}),-1.0]])]});}
            var Q1;
            Q1=makeQuery(id+"F6.boolean.opBoolean","MERGE",FACE,{"derivedFrom":[makeQuery(id+"F3.opExtrude","CAP_FACE",FACE,{"disambiguationData":[OSD([sQuery(id+"F2.wireOp",EDGE,"E3.bottom"),sQuery(id+"F2.wireOp",EDGE,"E3.top"),sQuery(id+"F2.wireOp",EDGE,"E3.left"),sQuery(id+"F2.wireOp",EDGE,"E3.right"),sQuery(id+"F2.wireOp",EDGE,"E4.top"),sQuery(id+"F2.wireOp",EDGE,"E4.left"),sQuery(id+"F2.wireOp",EDGE,"E4.right"),sQuery(id+"F2.wireOp",EDGE,"E5.top"),sQuery(id+"F2.wireOp",EDGE,"E5.left"),sQuery(id+"F2.wireOp",EDGE,"E5.right")])],"isStart":false}),makeQuery(id+"F6.opExtrude","CAP_FACE",FACE,{"disambiguationData":[OSD([sQuery(id+"F4.wireOp",EDGE,"E8.bottom"),sQuery(id+"F4.wireOp",EDGE,"E8.top"),sQuery(id+"F4.wireOp",EDGE,"E8.left"),sQuery(id+"F4.wireOp",EDGE,"E8.right")])],"isStart":false}),makeQuery(id+"F6.opExtrude","CAP_FACE",FACE,{"disambiguationData":[OSD([sQuery(id+"F4.wireOp",EDGE,"E9.bottom"),sQuery(id+"F4.wireOp",EDGE,"E9.top"),sQuery(id+"F4.wireOp",EDGE,"E9.left"),sQuery(id+"F4.wireOp",EDGE,"E9.right")])],"isStart":false}),makeQuery(id+"F6.opExtrude","CAP_FACE",FACE,{"disambiguationData":[OSD([sQuery(id+"F4.wireOp",EDGE,"E10.bottom"),sQuery(id+"F4.wireOp",EDGE,"E10.top"),sQuery(id+"F4.wireOp",EDGE,"E10.left"),sQuery(id+"F4.wireOp",EDGE,"E10.right")])],"isStart":false}),makeQuery(id+"F6.opExtrude","CAP_FACE",FACE,{"disambiguationData":[OSD([sQuery(id+"F4.wireOp",EDGE,"E11.bottom"),sQuery(id+"F4.wireOp",EDGE,"E11.top"),sQuery(id+"F4.wireOp",EDGE,"E11.left"),sQuery(id+"F4.wireOp",EDGE,"E11.right")])],"isStart":false}),makeQuery(id+"F6.opExtrude","CAP_FACE",FACE,{"disambiguationData":[OSD([sQuery(id+"F4.wireOp",EDGE,"E12.bottom"),sQuery(id+"F4.wireOp",EDGE,"E12.top"),sQuery(id+"F4.wireOp",EDGE,"E12.left"),sQuery(id+"F4.wireOp",EDGE,"E12.right")])],"isStart":false}),makeQuery(id+"F6.opExtrude","CAP_FACE",FACE,{"disambiguationData":[OSD([sQuery(id+"F4.wireOp",EDGE,"E13.bottom"),sQuery(id+"F4.wireOp",EDGE,"E13.top"),sQuery(id+"F4.wireOp",EDGE,"E13.left"),sQuery(id+"F4.wireOp",EDGE,"E13.right")])],"isStart":false})]});
            extrude(context, id + "F14", {"entities" : qUnion([Q0]), "operationType" : NewBodyOperationType.ADD, "endBound" : BoundingType.UP_TO_SURFACE, "endBoundEntityFace" : qUnion([Q1]), "depth" : 25.4 * mm});
        }
        {
            var Q0;
            Q0=makeQuery(id+"F14.boolean.opBoolean","MERGE",FACE,{"derivedFrom":[makeQuery(id+"F6.boolean.opBoolean","MERGE",FACE,{"derivedFrom":[makeQuery(id+"F3.opExtrude","CAP_FACE",FACE,{"disambiguationData":[OSD([sQuery(id+"F2.wireOp",EDGE,"E3.bottom"),sQuery(id+"F2.wireOp",EDGE,"E3.top"),sQuery(id+"F2.wireOp",EDGE,"E3.left"),sQuery(id+"F2.wireOp",EDGE,"E3.right"),sQuery(id+"F2.wireOp",EDGE,"E4.top"),sQuery(id+"F2.wireOp",EDGE,"E4.left"),sQuery(id+"F2.wireOp",EDGE,"E4.right"),sQuery(id+"F2.wireOp",EDGE,"E5.top"),sQuery(id+"F2.wireOp",EDGE,"E5.left"),sQuery(id+"F2.wireOp",EDGE,"E5.right")])],"isStart":false}),makeQuery(id+"F6.opExtrude","CAP_FACE",FACE,{"disambiguationData":[OSD([sQuery(id+"F4.wireOp",EDGE,"E8.bottom"),sQuery(id+"F4.wireOp",EDGE,"E8.top"),sQuery(id+"F4.wireOp",EDGE,"E8.left"),sQuery(id+"F4.wireOp",EDGE,"E8.right")])],"isStart":false}),makeQuery(id+"F6.opExtrude","CAP_FACE",FACE,{"disambiguationData":[OSD([sQuery(id+"F4.wireOp",EDGE,"E9.bottom"),sQuery(id+"F4.wireOp",EDGE,"E9.top"),sQuery(id+"F4.wireOp",EDGE,"E9.left"),sQuery(id+"F4.wireOp",EDGE,"E9.right")])],"isStart":false}),makeQuery(id+"F6.opExtrude","CAP_FACE",FACE,{"disambiguationData":[OSD([sQuery(id+"F4.wireOp",EDGE,"E10.bottom"),sQuery(id+"F4.wireOp",EDGE,"E10.top"),sQuery(id+"F4.wireOp",EDGE,"E10.left"),sQuery(id+"F4.wireOp",EDGE,"E10.right")])],"isStart":false}),makeQuery(id+"F6.opExtrude","CAP_FACE",FACE,{"disambiguationData":[OSD([sQuery(id+"F4.wireOp",EDGE,"E11.bottom"),sQuery(id+"F4.wireOp",EDGE,"E11.top"),sQuery(id+"F4.wireOp",EDGE,"E11.left"),sQuery(id+"F4.wireOp",EDGE,"E11.right")])],"isStart":false}),makeQuery(id+"F6.opExtrude","CAP_FACE",FACE,{"disambiguationData":[OSD([sQuery(id+"F4.wireOp",EDGE,"E12.bottom"),sQuery(id+"F4.wireOp",EDGE,"E12.top"),sQuery(id+"F4.wireOp",EDGE,"E12.left"),sQuery(id+"F4.wireOp",EDGE,"E12.right")])],"isStart":false}),makeQuery(id+"F6.opExtrude","CAP_FACE",FACE,{"disambiguationData":[OSD([sQuery(id+"F4.wireOp",EDGE,"E13.bottom"),sQuery(id+"F4.wireOp",EDGE,"E13.top"),sQuery(id+"F4.wireOp",EDGE,"E13.left"),sQuery(id+"F4.wireOp",EDGE,"E13.right")])],"isStart":false})]}),makeQuery(id+"F6.opExtrude","CAP_FACE",FACE,{"disambiguationData":[OSD([sQuery(id+"F4.wireOp",EDGE,"E14.bottom"),sQuery(id+"F4.wireOp",EDGE,"E14.top"),sQuery(id+"F4.wireOp",EDGE,"E14.left"),sQuery(id+"F4.wireOp",EDGE,"E14.right")])],"isStart":false}),makeQuery(id+"F14.opExtrude","CAP_FACE",FACE,{"disambiguationData":[OSD([sQuery(id+"F11.wireOp",EDGE,"E38.top"),sQuery(id+"F11.wireOp",EDGE,"E38.left"),sQuery(id+"F13.wireOp",EDGE,"E39"),sQuery(id+"F13.wireOp",EDGE,"E40"),sQuery(id+"F13.wireOp",EDGE,"E41"),sQuery(id+"F13.wireOp",EDGE,"E42"),sQuery(id+"F13.wireOp",EDGE,"E43"),sQuery(id+"F13.wireOp",EDGE,"E44")])],"isStart":false})]});
            var sketch = newSketch(context, id + "F15", { "sketchPlane" : qUnion([Q0])});
            skLineSegment(sketch, "E45.bottom", {"start": v(63.5, -63.5) * mm, "end": v(5688.63, -63.5) * mm});
            skLineSegment(sketch, "E45.top", {"start": v(76.2, -76.2) * mm, "end": v(5675.93, -76.2) * mm});
            skLineSegment(sketch, "E45.left", {"start": v(63.5, -63.5) * mm, "end": v(63.5, -76.2) * mm});
            skLineSegment(sketch, "E45.right", {"start": v(5688.63, -63.5) * mm, "end": v(5688.63, -76.2) * mm});
            skLineSegment(sketch, "E46.top", {"start": v(5688.63, -2019.3) * mm, "end": v(5675.93, -2019.3) * mm});
            skLineSegment(sketch, "E46.left", {"start": v(5688.63, -76.2) * mm, "end": v(5688.63, -2019.3) * mm});
            skLineSegment(sketch, "E46.right", {"start": v(5675.93, -76.2) * mm, "end": v(5675.93, -2019.3) * mm});
            skLineSegment(sketch, "E47.top", {"start": v(63.5, -5054.6) * mm, "end": v(76.2, -5054.6) * mm});
            skLineSegment(sketch, "E47.left", {"start": v(63.5, -76.2) * mm, "end": v(63.5, -5054.6) * mm});
            skLineSegment(sketch, "E47.right", {"start": v(76.2, -76.2) * mm, "end": v(76.2, -5054.6) * mm});
            skSolve(sketch);
        }
        {
            var Q0;
            Q0=makeQuery(id+"F15.imprint","IMPRINT",FACE,{"disambiguationData":[TD([[makeQuery(id+"F15.imprint","IMPRINT",EDGE,{"derivedFrom":sQuery(id+"F15.wireOp",EDGE,"E45.bottom")}),-1.0]])]});
            extrude(context, id + "F16", {"entities" : qUnion([Q0]), "operationType" : NewBodyOperationType.ADD, "depth" : 1778 * mm});
        }
        {
            var Q0;
            Q0=makeQuery(id+"F14.boolean.opBoolean","MERGE",FACE,{"derivedFrom":[makeQuery(id+"F6.boolean.opBoolean","MERGE",FACE,{"derivedFrom":[makeQuery(id+"F3.opExtrude","CAP_FACE",FACE,{"disambiguationData":[OSD([sQuery(id+"F2.wireOp",EDGE,"E3.bottom"),sQuery(id+"F2.wireOp",EDGE,"E3.top"),sQuery(id+"F2.wireOp",EDGE,"E3.left"),sQuery(id+"F2.wireOp",EDGE,"E3.right"),sQuery(id+"F2.wireOp",EDGE,"E4.top"),sQuery(id+"F2.wireOp",EDGE,"E4.left"),sQuery(id+"F2.wireOp",EDGE,"E4.right"),sQuery(id+"F2.wireOp",EDGE,"E5.top"),sQuery(id+"F2.wireOp",EDGE,"E5.left"),sQuery(id+"F2.wireOp",EDGE,"E5.right")])],"isStart":false}),makeQuery(id+"F6.opExtrude","CAP_FACE",FACE,{"disambiguationData":[OSD([sQuery(id+"F4.wireOp",EDGE,"E8.bottom"),sQuery(id+"F4.wireOp",EDGE,"E8.top"),sQuery(id+"F4.wireOp",EDGE,"E8.left"),sQuery(id+"F4.wireOp",EDGE,"E8.right")])],"isStart":false}),makeQuery(id+"F6.opExtrude","CAP_FACE",FACE,{"disambiguationData":[OSD([sQuery(id+"F4.wireOp",EDGE,"E9.bottom"),sQuery(id+"F4.wireOp",EDGE,"E9.top"),sQuery(id+"F4.wireOp",EDGE,"E9.left"),sQuery(id+"F4.wireOp",EDGE,"E9.right")])],"isStart":false}),makeQuery(id+"F6.opExtrude","CAP_FACE",FACE,{"disambiguationData":[OSD([sQuery(id+"F4.wireOp",EDGE,"E10.bottom"),sQuery(id+"F4.wireOp",EDGE,"E10.top"),sQuery(id+"F4.wireOp",EDGE,"E10.left"),sQuery(id+"F4.wireOp",EDGE,"E10.right")])],"isStart":false}),makeQuery(id+"F6.opExtrude","CAP_FACE",FACE,{"disambiguationData":[OSD([sQuery(id+"F4.wireOp",EDGE,"E11.bottom"),sQuery(id+"F4.wireOp",EDGE,"E11.top"),sQuery(id+"F4.wireOp",EDGE,"E11.left"),sQuery(id+"F4.wireOp",EDGE,"E11.right")])],"isStart":false}),makeQuery(id+"F6.opExtrude","CAP_FACE",FACE,{"disambiguationData":[OSD([sQuery(id+"F4.wireOp",EDGE,"E12.bottom"),sQuery(id+"F4.wireOp",EDGE,"E12.top"),sQuery(id+"F4.wireOp",EDGE,"E12.left"),sQuery(id+"F4.wireOp",EDGE,"E12.right")])],"isStart":false}),makeQuery(id+"F6.opExtrude","CAP_FACE",FACE,{"disambiguationData":[OSD([sQuery(id+"F4.wireOp",EDGE,"E13.bottom"),sQuery(id+"F4.wireOp",EDGE,"E13.top"),sQuery(id+"F4.wireOp",EDGE,"E13.left"),sQuery(id+"F4.wireOp",EDGE,"E13.right")])],"isStart":false})]}),makeQuery(id+"F6.opExtrude","CAP_FACE",FACE,{"disambiguationData":[OSD([sQuery(id+"F4.wireOp",EDGE,"E14.bottom"),sQuery(id+"F4.wireOp",EDGE,"E14.top"),sQuery(id+"F4.wireOp",EDGE,"E14.left"),sQuery(id+"F4.wireOp",EDGE,"E14.right")])],"isStart":false}),makeQuery(id+"F14.opExtrude","CAP_FACE",FACE,{"disambiguationData":[OSD([sQuery(id+"F11.wireOp",EDGE,"E38.top"),sQuery(id+"F11.wireOp",EDGE,"E38.left"),sQuery(id+"F13.wireOp",EDGE,"E39"),sQuery(id+"F13.wireOp",EDGE,"E40"),sQuery(id+"F13.wireOp",EDGE,"E41"),sQuery(id+"F13.wireOp",EDGE,"E42"),sQuery(id+"F13.wireOp",EDGE,"E43"),sQuery(id+"F13.wireOp",EDGE,"E44")])],"isStart":false})]});
            var sketch = newSketch(context, id + "F17", { "sketchPlane" : qUnion([Q0])});
            skLineSegment(sketch, "E48.bottom", {"start": v(-933.5, -723.9) * mm, "end": v(63.5, -723.9) * mm});
            skLineSegment(sketch, "E48.top", {"start": v(-933.5, -391.26) * mm, "end": v(63.5, -391.26) * mm});
            skLineSegment(sketch, "E48.left", {"start": v(-933.5, -723.9) * mm, "end": v(-933.5, -391.26) * mm});
            skLineSegment(sketch, "E49", {"start": v(63.5, -391.26) * mm, "end": v(63.5, -723.9) * mm});
            skSolve(sketch);
        }
        {
            var Q0;
            {var subQ6=sQuery(id+"F17.wireOp",EDGE,"E48.left");Q0=makeQuery(id+"F17.imprint","IMPRINT",FACE,{"disambiguationData":[TD([[makeQuery(id+"F17.imprint","IMPRINT",EDGE,{"derivedFrom":subQ6}),-1.0]])]});}
            var Q1;
            {var subQ27=sQuery(id+"F17.wireOp",EDGE,"E49");Q1=makeQuery(id+"F17.imprint","IMPRINT",FACE,{"disambiguationData":[TD([[makeQuery(id+"F17.imprint","IMPRINT",EDGE,{"derivedFrom":subQ27}),-1.0]])]});}
            extrude(context, id + "F18", {"entities" : qUnion([Q0, Q1]), "operationType" : NewBodyOperationType.ADD, "depth" : 25.4 * mm});
        }
        {
            var Q0;
            {var subQ0=sQuery(id+"F4.wireOp",EDGE,"E14.bottom");var subQ1=sQuery(id+"F4.wireOp",EDGE,"E14.top");var subQ2=sQuery(id+"F4.wireOp",EDGE,"E14.left");var subQ3=sQuery(id+"F4.wireOp",EDGE,"E14.right");var subQ4=sQuery(id+"F11.wireOp",EDGE,"E38.top");var subQ5=sQuery(id+"F11.wireOp",EDGE,"E38.left");var subQ6=sQuery(id+"F13.wireOp",EDGE,"E39");var subQ7=sQuery(id+"F13.wireOp",EDGE,"E42");var subQ8=sQuery(id+"F13.wireOp",EDGE,"E43");Q0=makeQuery(id+"F18.boolean.opBoolean","SPLIT",FACE,{"disambiguationData":[TD([makeQuery(id+"F5.opExtrude","SWEPT_FACE",FACE,{"disambiguationData":[OSD([subQ0])]})])],"derivedFrom":makeQuery(id+"F14.boolean.opBoolean","MERGE",FACE,{"derivedFrom":[makeQuery(id+"F6.boolean.opBoolean","MERGE",FACE,{"derivedFrom":[makeQuery(id+"F3.opExtrude","CAP_FACE",FACE,{"disambiguationData":[OSD([sQuery(id+"F2.wireOp",EDGE,"E3.bottom"),sQuery(id+"F2.wireOp",EDGE,"E3.top"),sQuery(id+"F2.wireOp",EDGE,"E3.left"),sQuery(id+"F2.wireOp",EDGE,"E3.right"),sQuery(id+"F2.wireOp",EDGE,"E4.top"),sQuery(id+"F2.wireOp",EDGE,"E4.left"),sQuery(id+"F2.wireOp",EDGE,"E4.right"),sQuery(id+"F2.wireOp",EDGE,"E5.top"),sQuery(id+"F2.wireOp",EDGE,"E5.left"),sQuery(id+"F2.wireOp",EDGE,"E5.right")])],"isStart":false}),makeQuery(id+"F6.opExtrude","CAP_FACE",FACE,{"disambiguationData":[OSD([sQuery(id+"F4.wireOp",EDGE,"E8.bottom"),sQuery(id+"F4.wireOp",EDGE,"E8.top"),sQuery(id+"F4.wireOp",EDGE,"E8.left"),sQuery(id+"F4.wireOp",EDGE,"E8.right")])],"isStart":false}),makeQuery(id+"F6.opExtrude","CAP_FACE",FACE,{"disambiguationData":[OSD([sQuery(id+"F4.wireOp",EDGE,"E9.bottom"),sQuery(id+"F4.wireOp",EDGE,"E9.top"),sQuery(id+"F4.wireOp",EDGE,"E9.left"),sQuery(id+"F4.wireOp",EDGE,"E9.right")])],"isStart":false}),makeQuery(id+"F6.opExtrude","CAP_FACE",FACE,{"disambiguationData":[OSD([sQuery(id+"F4.wireOp",EDGE,"E10.bottom"),sQuery(id+"F4.wireOp",EDGE,"E10.top"),sQuery(id+"F4.wireOp",EDGE,"E10.left"),sQuery(id+"F4.wireOp",EDGE,"E10.right")])],"isStart":false}),makeQuery(id+"F6.opExtrude","CAP_FACE",FACE,{"disambiguationData":[OSD([sQuery(id+"F4.wireOp",EDGE,"E11.bottom"),sQuery(id+"F4.wireOp",EDGE,"E11.top"),sQuery(id+"F4.wireOp",EDGE,"E11.left"),sQuery(id+"F4.wireOp",EDGE,"E11.right")])],"isStart":false}),makeQuery(id+"F6.opExtrude","CAP_FACE",FACE,{"disambiguationData":[OSD([sQuery(id+"F4.wireOp",EDGE,"E12.bottom"),sQuery(id+"F4.wireOp",EDGE,"E12.top"),sQuery(id+"F4.wireOp",EDGE,"E12.left"),sQuery(id+"F4.wireOp",EDGE,"E12.right")])],"isStart":false}),makeQuery(id+"F6.opExtrude","CAP_FACE",FACE,{"disambiguationData":[OSD([sQuery(id+"F4.wireOp",EDGE,"E13.bottom"),sQuery(id+"F4.wireOp",EDGE,"E13.top"),sQuery(id+"F4.wireOp",EDGE,"E13.left"),sQuery(id+"F4.wireOp",EDGE,"E13.right")])],"isStart":false})]}),makeQuery(id+"F6.opExtrude","CAP_FACE",FACE,{"disambiguationData":[OSD([subQ0,subQ1,subQ2,subQ3])],"isStart":false}),makeQuery(id+"F14.opExtrude","CAP_FACE",FACE,{"disambiguationData":[OSD([subQ4,subQ5,subQ6,sQuery(id+"F13.wireOp",EDGE,"E40"),sQuery(id+"F13.wireOp",EDGE,"E41"),subQ7,subQ8,sQuery(id+"F13.wireOp",EDGE,"E44")])],"isStart":false})]})});}
            var sketch = newSketch(context, id + "F19", { "sketchPlane" : qUnion([Q0])});
            skLineSegment(sketch, "E50", {"start": v(-886.35, -723.9) * mm, "end": v(-886.35, -429.36) * mm});
            skLineSegment(sketch, "E51", {"start": v(-886.35, -429.36) * mm, "end": v(63.5, -429.36) * mm});
            skLineSegment(sketch, "E52", {"start": v(63.5, -429.36) * mm, "end": v(63.5, -467.46) * mm});
            skLineSegment(sketch, "E53", {"start": v(63.5, -467.46) * mm, "end": v(-838.7, -467.46) * mm});
            skLineSegment(sketch, "E54", {"start": v(-838.7, -467.46) * mm, "end": v(-838.7, -723.9) * mm});
            skLineSegment(sketch, "E55", {"start": v(-886.35, -723.9) * mm, "end": v(-838.7, -723.9) * mm});
            skSolve(sketch);
        }
        {
            var Q0;
            Q0=makeQuery(id+"F19.imprint","IMPRINT",FACE,{"disambiguationData":[TD([[makeQuery(id+"F19.imprint","IMPRINT",EDGE,{"derivedFrom":sQuery(id+"F19.wireOp",EDGE,"E50")}),-1.0]])]});
            var Q1;
            Q1=makeQuery(id+"F19.imprint","IMPRINT",FACE,{"disambiguationData":[TD([[makeQuery(id+"F19.imprint","IMPRINT",EDGE,{"derivedFrom":sQuery(id+"F19.wireOp",EDGE,"E55")}),-1.0]])]});
            extrude(context, id + "F20", {"entities" : qUnion([Q0, Q1]), "operationType" : NewBodyOperationType.ADD, "depth" : 228.6 * mm});
        }
        {
            var Q0;
            Q0=makeQuery(id+"F20.opExtrude","CAP_FACE",FACE,{"disambiguationData":[OSD([sQuery(id+"F4.wireOp",EDGE,"E14.bottom"),sQuery(id+"F4.wireOp",EDGE,"E14.top"),sQuery(id+"F4.wireOp",EDGE,"E14.left"),sQuery(id+"F4.wireOp",EDGE,"E14.right"),sQuery(id+"F11.wireOp",EDGE,"E38.bottom"),sQuery(id+"F11.wireOp",EDGE,"E38.top"),sQuery(id+"F11.wireOp",EDGE,"E38.left"),sQuery(id+"F13.wireOp",EDGE,"E39"),sQuery(id+"F13.wireOp",EDGE,"E43"),sQuery(id+"F19.wireOp",EDGE,"E50"),sQuery(id+"F19.wireOp",EDGE,"E51"),sQuery(id+"F19.wireOp",EDGE,"E52"),sQuery(id+"F19.wireOp",EDGE,"E53"),sQuery(id+"F19.wireOp",EDGE,"E54")])],"isStart":false});
            var sketch = newSketch(context, id + "F21", { "sketchPlane" : qUnion([Q0])});
            skLineSegment(sketch, "E56.bottom", {"start": v(-933.5, -467.46) * mm, "end": v(63.5, -467.46) * mm});
            skLineSegment(sketch, "E56.top", {"start": v(-933.5, -99.16) * mm, "end": v(63.5, -99.16) * mm});
            skLineSegment(sketch, "E56.left", {"start": v(-933.5, -467.46) * mm, "end": v(-933.5, -99.16) * mm});
            skLineSegment(sketch, "E56.right", {"start": v(63.5, -467.46) * mm, "end": v(63.5, -99.16) * mm});
            skSolve(sketch);
        }
        {
            var Q0;
            {var subQ5=sQuery(id+"F21.wireOp",EDGE,"E56.top");Q0=makeQuery(id+"F21.imprint","IMPRINT",FACE,{"disambiguationData":[TD([[makeQuery(id+"F21.imprint","IMPRINT",EDGE,{"derivedFrom":subQ5}),-1.0]])]});}
            var Q1;
            {var subQ3=makeQuery(id+"F20.opExtrude","CAP_EDGE",EDGE,{"disambiguationData":[OSD([sQuery(id+"F19.wireOp",EDGE,"E51")])],"isStart":false});Q1=makeQuery(id+"F21.imprint","IMPRINT",FACE,{"disambiguationData":[TD([[makeQuery(id+"F21.imprint","IMPRINT",EDGE,{"derivedFrom":subQ3}),-1.0]])]});}
            extrude(context, id + "F22", {"entities" : qUnion([Q0, Q1]), "operationType" : NewBodyOperationType.ADD, "depth" : 25.4 * mm});
        }
        {
            var Q0;
            Q0=makeQuery(id+"F20.opExtrude","CAP_FACE",FACE,{"disambiguationData":[OSD([sQuery(id+"F4.wireOp",EDGE,"E14.bottom"),sQuery(id+"F4.wireOp",EDGE,"E14.top"),sQuery(id+"F4.wireOp",EDGE,"E14.left"),sQuery(id+"F4.wireOp",EDGE,"E14.right"),sQuery(id+"F11.wireOp",EDGE,"E38.bottom"),sQuery(id+"F11.wireOp",EDGE,"E38.top"),sQuery(id+"F11.wireOp",EDGE,"E38.left"),sQuery(id+"F13.wireOp",EDGE,"E39"),sQuery(id+"F13.wireOp",EDGE,"E43"),sQuery(id+"F19.wireOp",EDGE,"E50"),sQuery(id+"F19.wireOp",EDGE,"E51"),sQuery(id+"F19.wireOp",EDGE,"E52"),sQuery(id+"F19.wireOp",EDGE,"E53"),sQuery(id+"F19.wireOp",EDGE,"E54")])],"isStart":false});
            extrude(context, id + "F23", {"entities" : qUnion([Q0]), "operationType" : NewBodyOperationType.ADD, "depth" : 228.6 * mm});
        }
        {
            var Q0;
            Q0=makeQuery(id+"F22.opExtrude","CAP_FACE",FACE,{"disambiguationData":[OSD([sQuery(id+"F21.wireOp",EDGE,"E56.bottom"),sQuery(id+"F21.wireOp",EDGE,"E56.top"),sQuery(id+"F21.wireOp",EDGE,"E56.left"),sQuery(id+"F21.wireOp",EDGE,"E56.right")])],"isStart":false});
            var sketch = newSketch(context, id + "F24", { "sketchPlane" : qUnion([Q0])});
            skLineSegment(sketch, "E57", {"start": v(-886.35, -467.46) * mm, "end": v(-886.35, -137.26) * mm});
            skLineSegment(sketch, "E58", {"start": v(-886.35, -137.26) * mm, "end": v(63.5, -137.26) * mm});
            skLineSegment(sketch, "E59", {"start": v(63.5, -137.26) * mm, "end": v(63.5, -175.36) * mm});
            skLineSegment(sketch, "E60", {"start": v(63.5, -175.36) * mm, "end": v(-838.7, -175.36) * mm});
            skLineSegment(sketch, "E61", {"start": v(-838.7, -175.36) * mm, "end": v(-838.7, -467.46) * mm});
            skLineSegment(sketch, "E62", {"start": v(-838.7, -467.46) * mm, "end": v(-886.35, -467.46) * mm});
            skSolve(sketch);
        }
        {
            var Q0;
            Q0=makeQuery(id+"F24.imprint","IMPRINT",FACE,{"disambiguationData":[TD([[makeQuery(id+"F24.imprint","IMPRINT",EDGE,{"derivedFrom":sQuery(id+"F24.wireOp",EDGE,"E57")}),-1.0]])]});
            var Q1;
            Q1=makeQuery(id+"F23.opExtrude","CAP_FACE",FACE,{"disambiguationData":[OSD([sQuery(id+"F4.wireOp",EDGE,"E14.bottom"),sQuery(id+"F4.wireOp",EDGE,"E14.top"),sQuery(id+"F4.wireOp",EDGE,"E14.left"),sQuery(id+"F4.wireOp",EDGE,"E14.right"),sQuery(id+"F11.wireOp",EDGE,"E38.bottom"),sQuery(id+"F11.wireOp",EDGE,"E38.top"),sQuery(id+"F11.wireOp",EDGE,"E38.left"),sQuery(id+"F13.wireOp",EDGE,"E39"),sQuery(id+"F13.wireOp",EDGE,"E43"),sQuery(id+"F19.wireOp",EDGE,"E50"),sQuery(id+"F19.wireOp",EDGE,"E51"),sQuery(id+"F19.wireOp",EDGE,"E52"),sQuery(id+"F19.wireOp",EDGE,"E53"),sQuery(id+"F19.wireOp",EDGE,"E54")])],"isStart":false});
            extrude(context, id + "F25", {"entities" : qUnion([Q0]), "operationType" : NewBodyOperationType.ADD, "endBound" : BoundingType.UP_TO_SURFACE, "endBoundEntityFace" : qUnion([Q1]), "depth" : 25.4 * mm});
        }
        {
            var Q0;
            Q0=makeQuery(id+"F16.opExtrude","SWEPT_FACE",FACE,{"disambiguationData":[OSD([sQuery(id+"F15.wireOp",EDGE,"E45.bottom")])]});
            var sketch = newSketch(context, id + "F26", { "sketchPlane" : qUnion([Q0])});
            skLineSegment(sketch, "E63", {"start": v(63.5, -707.74) * mm, "end": v(5439.41, -1981.2) * mm});
            skLineSegment(sketch, "E64", {"start": v(5439.41, -1981.2) * mm, "end": v(63.5, -1981.2) * mm});
            skLineSegment(sketch, "E65", {"start": v(63.5, -1981.2) * mm, "end": v(63.5, -707.74) * mm});
            skSolve(sketch);
        }
        {
            var Q0;
            Q0=makeQuery(id+"F26.imprint","IMPRINT",FACE,{"disambiguationData":[TD([[makeQuery(id+"F26.imprint","IMPRINT",EDGE,{"derivedFrom":sQuery(id+"F26.wireOp",EDGE,"E63")}),-1.0]])]});
            extrude(context, id + "F27", {"entities" : qUnion([Q0]), "operationType" : NewBodyOperationType.REMOVE, "endBound" : BoundingType.UP_TO_NEXT, "oppositeDirection" : true, "depth" : 25.4 * mm});
        }
    });
